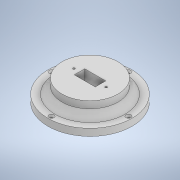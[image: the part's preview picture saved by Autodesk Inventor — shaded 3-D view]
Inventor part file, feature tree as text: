
AUTODESK INVENTOR PART (.ipt)
format: ipt  version: 2022 (Build 260153000, 153)  size: 170,496 bytes
history: native  units: mm
features: extrude x8, sketch x8, chamfer x1
ambient origin geometry x8: Origin, YZ Plane, XZ Plane, XY Plane, X Axis, Y Axis, Z Axis, Center Point
bodies: Solid1 (feature_tree)
feature tree (17):
  extrude  "Extrusion1"  Depth=10.0mm TaperAngle=0.0deg
  extrude  "Extrusion2"  Depth=10.0mm TaperAngle=0.0deg
  chamfer  "Chamfer1"  Distance=10.0mm Angle=45.0deg
  extrude  "Extrusion3"  Depth=10.0mm TaperAngle=0.0deg
  extrude  "Extrusion4"  Depth=10.0mm TaperAngle=0.0deg
  extrude  "Extrusion5"  Depth=55.0mm
  extrude  "Extrusion6"  Depth=40.0mm
  extrude  "Extrusion7"  Depth=55.0mm
  extrude  "Extrusion8"  TaperAngle=0.0deg  [1 undecoded]
  sketch  "Sketch1"  dims[d0=110.0mm d1=10.0mm d2=0.0mm]
  sketch  "Sketch2"  dims[d3=100.0mm d4=10.0mm d5=0.0mm d6=10.0mm d7=2.0mm d8=45.0deg]
  sketch  "Sketch3"  dims[d9=80.0mm d10=10.0mm d11=0.0mm]
  sketch  "Sketch4"  dims[d12=120.0mm d13=10.0mm d14=0.0mm]
  sketch  "Sketch5"  dims[d15=7.25mm d16=55.0mm]
  sketch  "Sketch6"  dims[d17=40.0mm d19=360.0deg d21=2.1735mm d22=-7.853982mm]
  sketch  "Sketch7"  dims[d23=2.903mm d24=55.0mm]
  sketch  "Sketch8"  dims[d25=40.0mm d27=360.0deg d29=0.0mm d30=0.0mm d31=30.0mm d32=15.0mm d33=0.0mm d34=0.0mm d35=2.903mm d36=23.0mm d37=20.0mm d39=360.0deg d41=0.0mm d42=0.0mm]
note: 1 required parameter value undecoded (feature->parameter linkage not recoverable at this tier; creation-order binding heuristic only, values carry confidence <= 0.55)
